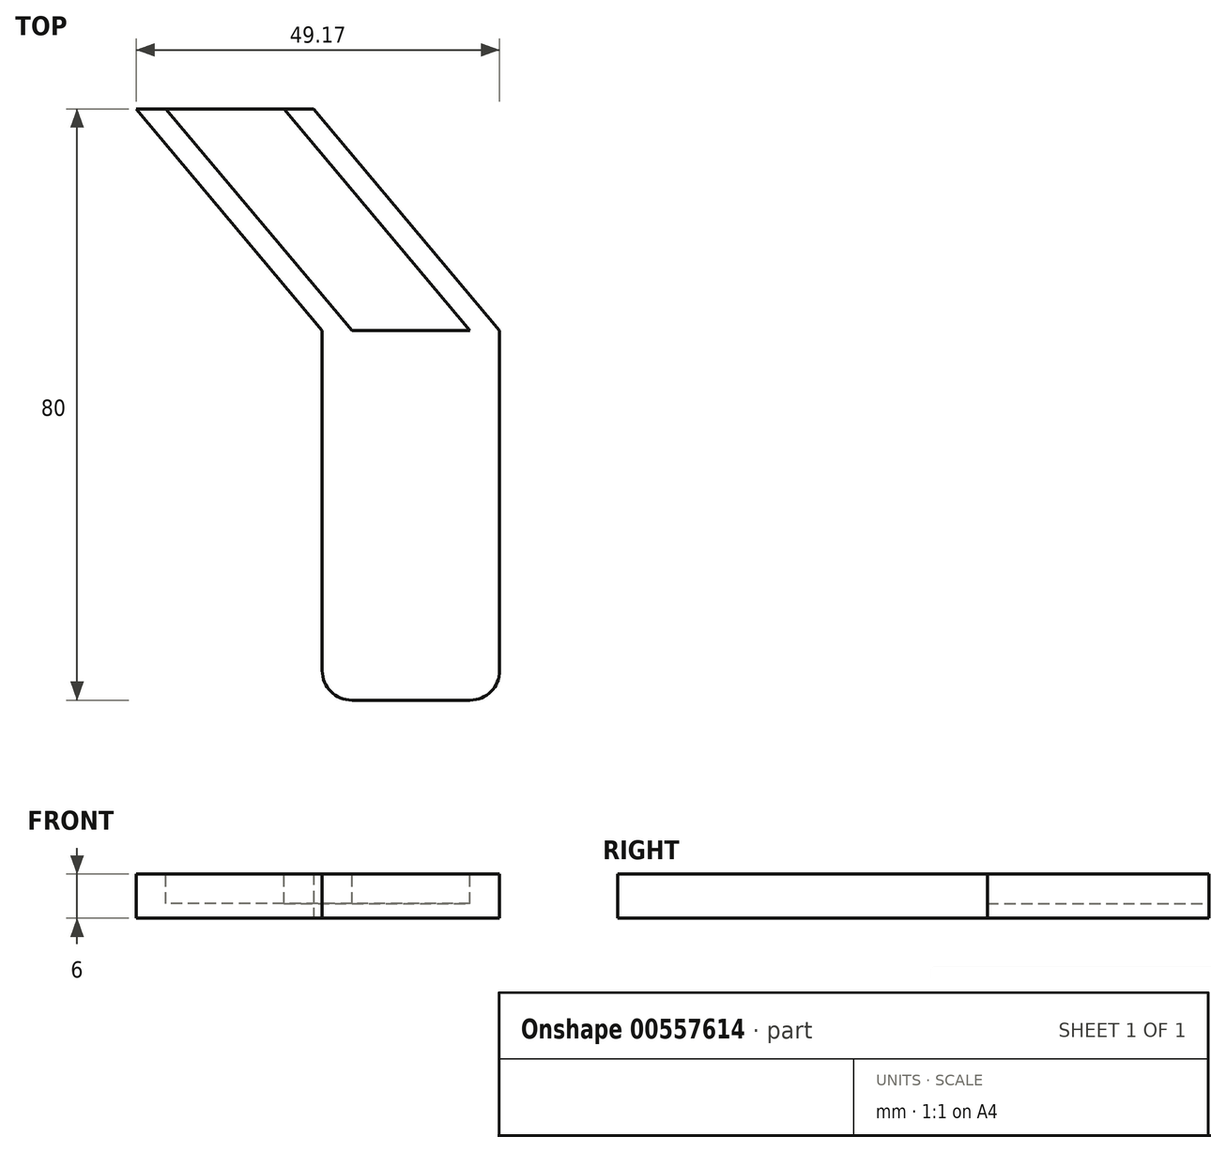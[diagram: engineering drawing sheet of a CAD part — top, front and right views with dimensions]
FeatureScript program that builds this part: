
annotation { "Feature Type Name" : "Feature", "Feature Type Description" : "" }
export const myFeature = defineFeature(function(context is Context, id is Id, definition is map)
    precondition{}
    {
        {
            var Q0;
            Q0=qCreatedBy(makeId("Top.planeOp"),FACE);
            var sketch = newSketch(context, id + "F0", { "sketchPlane" : qUnion([Q0])});
            skLineSegment(sketch, "E0", {"start": v(49.17, -76) * mm, "end": v(49.17, -30) * mm});
            skLineSegment(sketch, "E1", {"start": v(49.17, -30) * mm, "end": v(24, 0) * mm});
            skLineSegment(sketch, "E2", {"start": v(24, 0) * mm, "end": v(0, 0) * mm});
            skLineSegment(sketch, "E3", {"start": v(0, 0) * mm, "end": v(25.17, -30) * mm});
            skLineSegment(sketch, "E4", {"start": v(25.17, -30) * mm, "end": v(25.17, -76) * mm});
            skLineSegment(sketch, "E5", {"start": v(29.17, -80) * mm, "end": v(45.17, -80) * mm});
            skPoint(sketch, "E6.visualSharp", {"position": v(25.17, -80) * mm});
            skArc(sketch, "E6.filletArc", {"start": v(25.17, -76) * mm, "mid": v(26.34, -78.83) * mm, "end": v(29.17, -80) * mm});
            skPoint(sketch, "E7.visualSharp", {"position": v(49.17, -80) * mm});
            skArc(sketch, "E7.filletArc", {"start": v(45.17, -80) * mm, "mid": v(48, -78.83) * mm, "end": v(49.17, -76) * mm});
            skSolve(sketch);
        }
        {
            var Q0;
            Q0=makeQuery(id+"F0.imprint","IMPRINT",FACE,{"disambiguationData":[TD([[makeQuery(id+"F0.imprint","IMPRINT",EDGE,{"derivedFrom":sQuery(id+"F0.wireOp",EDGE,"E0")}),1.0]])]});
            extrude(context, id + "F1", {"entities" : qUnion([Q0]), "depth" : 6 * mm, "offsetDistance" : 25 * mm});
        }
        {
            var Q0;
            Q0=makeQuery(id+"F1.opExtrude","CAP_FACE",FACE,{"disambiguationData":[OSD([sQuery(id+"F0.wireOp",EDGE,"E0"),sQuery(id+"F0.wireOp",EDGE,"E1"),sQuery(id+"F0.wireOp",EDGE,"E2"),sQuery(id+"F0.wireOp",EDGE,"E3"),sQuery(id+"F0.wireOp",EDGE,"E4"),sQuery(id+"F0.wireOp",EDGE,"E5"),sQuery(id+"F0.wireOp",EDGE,"E6.filletArc"),sQuery(id+"F0.wireOp",EDGE,"E7.filletArc")])],"isStart":false});
            var sketch = newSketch(context, id + "F2", { "sketchPlane" : qUnion([Q0])});
            skLineSegment(sketch, "E8", {"start": v(29.17, -30) * mm, "end": v(4, 0) * mm});
            skLineSegment(sketch, "E9", {"start": v(4, 0) * mm, "end": v(20, 0) * mm});
            skLineSegment(sketch, "E10", {"start": v(20, 0) * mm, "end": v(45.17, -30) * mm});
            skLineSegment(sketch, "E11", {"start": v(45.17, -30) * mm, "end": v(29.17, -30) * mm});
            skSolve(sketch);
        }
        {
            var Q0;
            Q0=makeQuery(id+"F2.imprint","IMPRINT",FACE,{"disambiguationData":[TD([[makeQuery(id+"F2.imprint","IMPRINT",EDGE,{"derivedFrom":sQuery(id+"F2.wireOp",EDGE,"E8")}),-1.0]])]});
            extrude(context, id + "F3", {"entities" : qUnion([Q0]), "operationType" : NewBodyOperationType.REMOVE, "oppositeDirection" : true, "depth" : 4 * mm, "offsetDistance" : 25 * mm});
        }
    });
